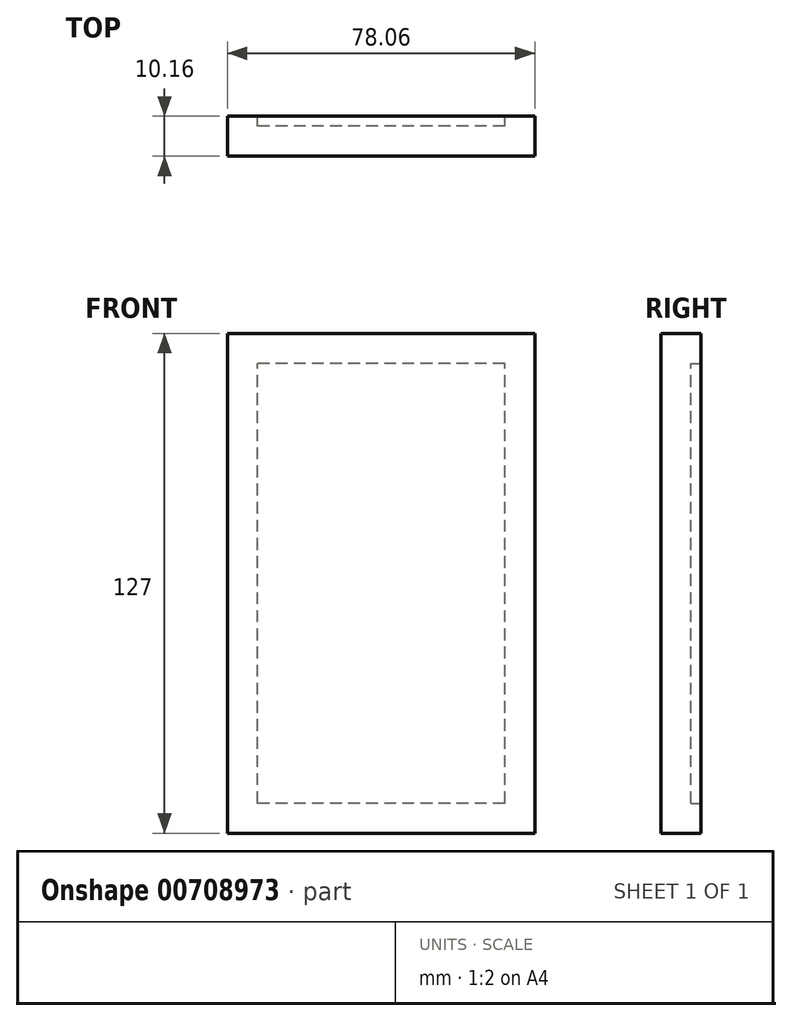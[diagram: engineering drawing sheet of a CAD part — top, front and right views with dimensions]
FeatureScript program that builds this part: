
annotation { "Feature Type Name" : "Feature", "Feature Type Description" : "" }
export const myFeature = defineFeature(function(context is Context, id is Id, definition is map)
    precondition{}
    {
        {
            var Q0;
            Q0=qCreatedBy(makeId("Front.planeOp"),FACE);
            var sketch = newSketch(context, id + "F0", { "sketchPlane" : qUnion([Q0])});
            skLineSegment(sketch, "E0.bottom", {"start": v(39.03, -63.5) * mm, "end": v(-39.03, -63.5) * mm});
            skLineSegment(sketch, "E0.top", {"start": v(39.03, 63.5) * mm, "end": v(-39.03, 63.5) * mm});
            skLineSegment(sketch, "E0.left", {"start": v(39.03, -63.5) * mm, "end": v(39.03, 63.5) * mm});
            skLineSegment(sketch, "E0.right", {"start": v(-39.03, -63.5) * mm, "end": v(-39.03, 63.5) * mm});
            skPoint(sketch, "E0.middle", {"position": v(0, 0) * mm});
            skSolve(sketch);
        }
        {
            var Q0;
            Q0=qSketchRegion(id+"F0",true);
            extrude(context, id + "F1", {"entities" : qUnion([Q0]), "depth" : 10.16 * mm, "offsetDistance" : 25.4 * mm});
        }
        {
            var Q0;
            Q0=makeQuery(id+"F1.opExtrude","CAP_FACE",FACE,{"disambiguationData":[OSD([sQuery(id+"F0.wireOp",EDGE,"E0.bottom"),sQuery(id+"F0.wireOp",EDGE,"E0.top"),sQuery(id+"F0.wireOp",EDGE,"E0.left"),sQuery(id+"F0.wireOp",EDGE,"E0.right")])],"isStart":true});
            shell(context, id + "F2", {"entities" : qUnion([Q0]), "thickness" : 7.62 * mm});
        }
    });
